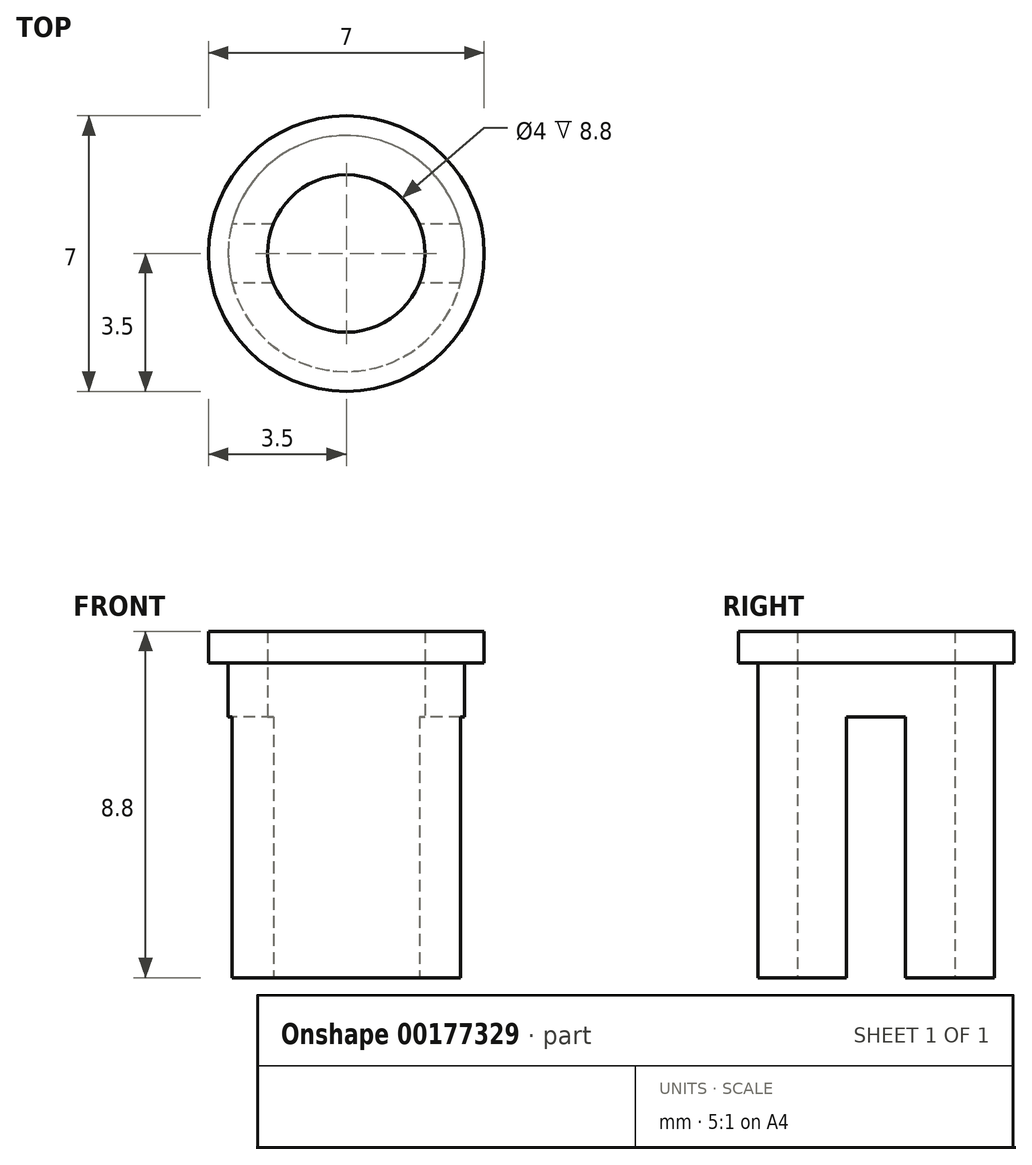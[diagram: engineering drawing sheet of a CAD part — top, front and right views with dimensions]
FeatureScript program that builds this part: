
annotation { "Feature Type Name" : "Feature", "Feature Type Description" : "" }
export const myFeature = defineFeature(function(context is Context, id is Id, definition is map)
    precondition{}
    {
        {
            var Q0;
            Q0=qCreatedBy(makeId("Right.planeOp"),FACE);
            var sketch = newSketch(context, id + "F0", { "sketchPlane" : qUnion([Q0])});
            skLineSegment(sketch, "E0", {"start": v(0, 0) * mm, "end": v(0, 8.57) * mm, "construction": true});
            skLineSegment(sketch, "E1", {"start": v(2, 0) * mm, "end": v(2, 8.8) * mm});
            skLineSegment(sketch, "E2", {"start": v(2, 8.8) * mm, "end": v(3.5, 8.8) * mm});
            skLineSegment(sketch, "E3", {"start": v(3.5, 8.8) * mm, "end": v(3.5, 8) * mm});
            skLineSegment(sketch, "E4", {"start": v(3.5, 8) * mm, "end": v(3, 8) * mm});
            skLineSegment(sketch, "E5", {"start": v(3, 8) * mm, "end": v(3, 0) * mm});
            skLineSegment(sketch, "E6", {"start": v(3, 0) * mm, "end": v(2, 0) * mm});
            skSolve(sketch);
        }
        {
            var Q0;
            Q0 = qSketchRegion(id + "F0", true);
            var Q1;
            Q1=sQuery(id+"F0.wireOp",EDGE,"E0");
            revolve(context, id + "F1", {"surfaceOperationType" : NewSurfaceOperationType.NEW, "entities" : qUnion([Q0]), "axis" : qUnion([Q1]), "revolveType" : RevolveType.FULL});
        }
        {
            var Q0;
            Q0=makeQuery(id+"F1.opRevolve","SWEPT_FACE",FACE,{"disambiguationData":[OSD([sQuery(id+"F0.wireOp",EDGE,"E6")])]});
            var sketch = newSketch(context, id + "F2", { "sketchPlane" : qUnion([Q0])});
            skLineSegment(sketch, "E7.bottom", {"start": v(4, 0.75) * mm, "end": v(-4, 0.75) * mm});
            skLineSegment(sketch, "E7.top", {"start": v(4, -0.75) * mm, "end": v(-4, -0.75) * mm});
            skLineSegment(sketch, "E7.left", {"start": v(4, 0.75) * mm, "end": v(4, -0.75) * mm});
            skLineSegment(sketch, "E7.right", {"start": v(-4, 0.75) * mm, "end": v(-4, -0.75) * mm});
            skPoint(sketch, "E7.middle", {"position": v(0, 0) * mm});
            skSolve(sketch);
        }
        {
            var Q0;
            Q0 = qSketchRegion(id + "F2", true);
            extrude(context, id + "F3", {"entities" : qUnion([Q0]), "operationType" : NewBodyOperationType.REMOVE, "oppositeDirection" : true, "depth" : 6.63 * mm, "offsetDistance" : 25 * mm});
        }
    });
